# Revit family: HVAC_Ductwork_Airzone_Square-Diffuser_DFCU-PX1
name_source: partatom
category: Air Terminals
revit_build: Autodesk Revit 2016 (Build: 20161004_0715(x64)
units: mm (PartAtom-declared; Revit-internal decimal feet)

## family parameters
Always vertical = Yes
Cut with Voids When Loaded = No
OmniClass Number = 23.75.70.21.27.11
OmniClass Title = Diffusers, Registers, and Grilles
Part Type = Normal
Room Calculation Point = Yes
Round Connector Dimension = Use Diameter
Shared = No
Work Plane-Based = No

## types (1)
- INVALID TYPE - Use Load Family and Type Catalog instead
    Accessories Material = Metal - AIRZONE - Aluminium - Brushed
    Ak = 1
    Compatible Accesories = Insulated flexible duct (TFTA) and non-insulated flexible duct (TFST)
    Description = Square diffuser with plenum
    Diffuser Nominal Diameter = 150 mm
    Disclaimer = All information provided in this model is reviewed before being published. However, Airzone cannot guarantee this model is error-free, therefore users are strongly encouraged to check for technical documentation and updates
    Duct Diameter = 125 mm
    Effective Area = 100.00 cm²
    Finish = White (RAL 9010)
    Fixing = Plenum-Wall hanging fixing by Rod; Diffuser-Plenum fixing by Screw
    Long Description = Square diffuser DFCU-PX with plenum that enables the air flow supply in four directions. Plenum made in galvanized Steel. Mechanical flow regulation. Lateral connection for round ducts.
    Main Material = Metal - AIRZONE - Extruded Aluminium - White (RAL 9010)
    Manufacturer = AIRZONE
    Max Flow = 600 m³/h
    Min Flow = 100 m³/h
    Model = INVALID – Type not loaded via type catalog
    Plenum Height = 180 mm
    Plenum Material = Metal - AIRZONE - Galvanized Sheet - Semi-polished
    Plenum Width = 175 mm
    Product Code = INVALID – Type not loaded via type catalog
    Product Comments = Refer to technical documentation for further details
    Product Documentation Download URL = http://doc.airzone.es
    Revit Model Version = 1.0
    Type Image Comments = Image available in product documentation download
    URL = www.airzone.es
    c1 = 0.000467
    c2 = -1.993
    c3 = -74.54
    c4 = -32.51
    c5 = 47.12
    c6 = -1.462
    c7 = 0.007003
    c8 = -0.483

## geometry (parser evidence)
native form markers: Sweep x6
no freeform markers — native parametric forms only
